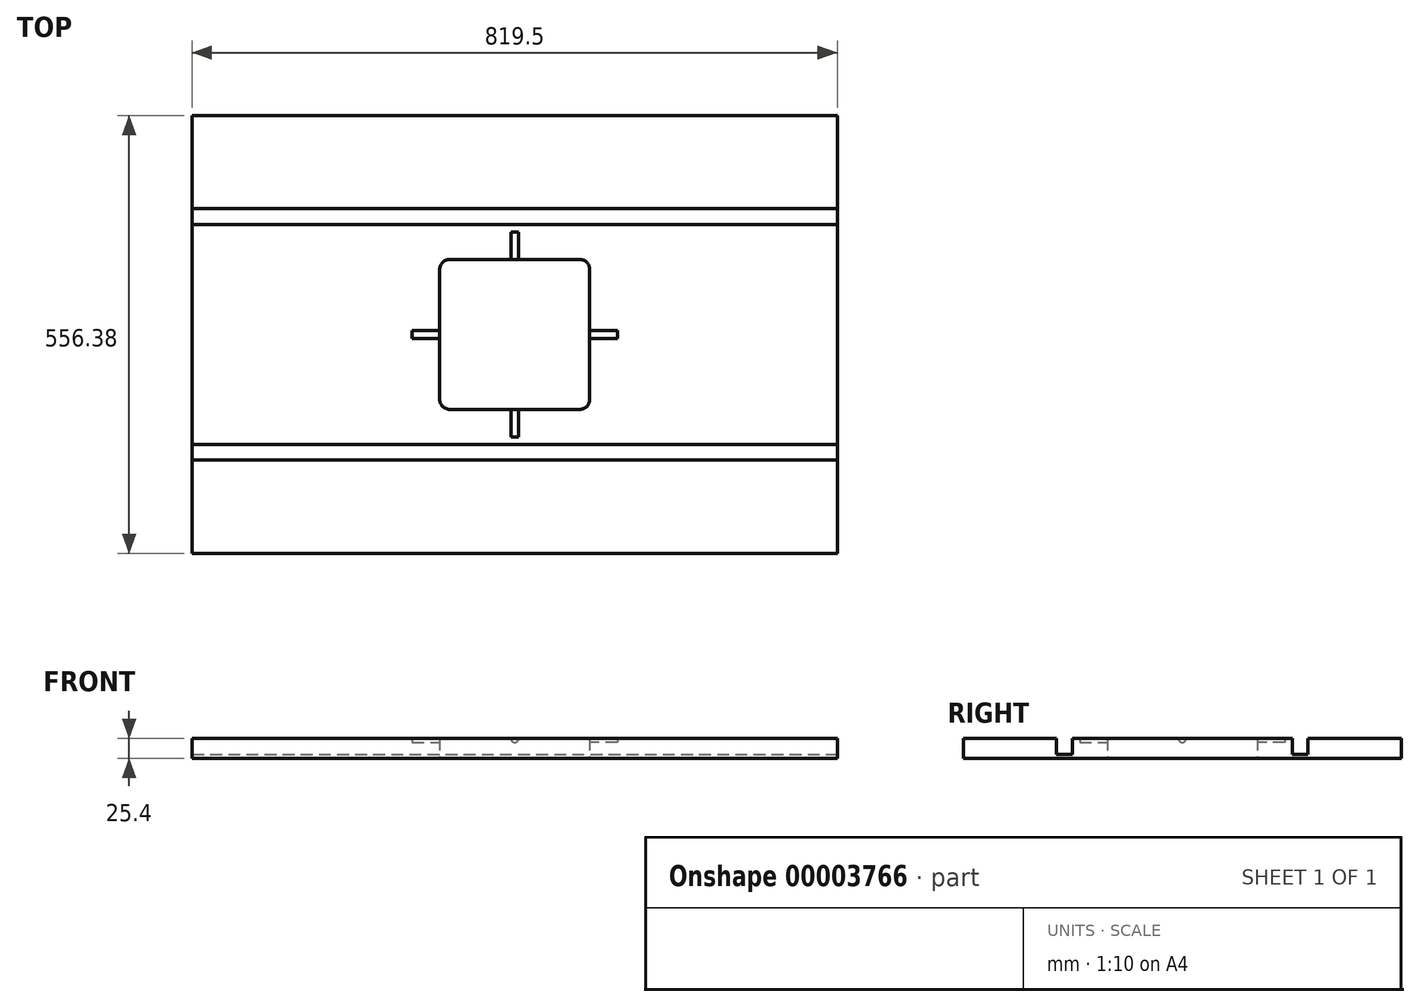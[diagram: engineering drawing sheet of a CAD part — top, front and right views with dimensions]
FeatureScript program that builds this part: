
annotation { "Feature Type Name" : "Feature", "Feature Type Description" : "" }
export const myFeature = defineFeature(function(context is Context, id is Id, definition is map)
    precondition{}
    {
        {
            var Q0;
            Q0=qCreatedBy(makeId("Top.planeOp"),FACE);
            var sketch = newSketch(context, id + "F0", { "sketchPlane" : qUnion([Q0])});
            skLineSegment(sketch, "E0.rect.bottom", {"start": v(-82.55, 95.25) * mm, "end": v(82.55, 95.25) * mm});
            skLineSegment(sketch, "E0.rect.top", {"start": v(-82.55, -95.25) * mm, "end": v(82.55, -95.25) * mm});
            skLineSegment(sketch, "E0.rect.left", {"start": v(-95.25, 82.55) * mm, "end": v(-95.25, -82.55) * mm});
            skLineSegment(sketch, "E0.rect.right", {"start": v(95.25, 82.55) * mm, "end": v(95.25, -82.55) * mm});
            skPoint(sketch, "E0.rect.middle", {"position": v(0, 0) * mm});
            skPoint(sketch, "E1.visualSharp", {"position": v(-95.25, 95.25) * mm});
            skArc(sketch, "E1.filletArc", {"start": v(-82.55, 95.25) * mm, "mid": v(-91.53, 91.53) * mm, "end": v(-95.25, 82.55) * mm});
            skPoint(sketch, "E2.visualSharp", {"position": v(-95.25, -95.25) * mm});
            skArc(sketch, "E2.filletArc", {"start": v(-95.25, -82.55) * mm, "mid": v(-91.53, -91.53) * mm, "end": v(-82.55, -95.25) * mm});
            skPoint(sketch, "E3.visualSharp", {"position": v(95.25, 95.25) * mm});
            skArc(sketch, "E3.filletArc", {"start": v(95.25, 82.55) * mm, "mid": v(91.53, 91.53) * mm, "end": v(82.55, 95.25) * mm});
            skPoint(sketch, "E4.visualSharp", {"position": v(95.25, -95.25) * mm});
            skArc(sketch, "E4.filletArc", {"start": v(82.55, -95.25) * mm, "mid": v(91.53, -91.53) * mm, "end": v(95.25, -82.55) * mm});
            skLineSegment(sketch, "E5.rect.bottom", {"start": v(-409.75, 278.2) * mm, "end": v(409.75, 278.2) * mm});
            skLineSegment(sketch, "E5.rect.top", {"start": v(-409.75, -278.2) * mm, "end": v(409.75, -278.2) * mm});
            skLineSegment(sketch, "E5.rect.left", {"start": v(-409.75, 278.2) * mm, "end": v(-409.75, -278.2) * mm});
            skLineSegment(sketch, "E5.rect.right", {"start": v(409.75, 278.2) * mm, "end": v(409.75, -278.2) * mm});
            skLineSegment(sketch, "E6", {"start": v(0, -95.25) * mm, "end": v(0, 95.25) * mm, "construction": true});
            skLineSegment(sketch, "E7", {"start": v(0, 0) * mm, "end": v(-95.25, 0) * mm, "construction": true});
            skLineSegment(sketch, "E8", {"start": v(0, 0) * mm, "end": v(95.25, 0) * mm, "construction": true});
            skSolve(sketch);
        }
        {
            var Q0;
            Q0=makeQuery(id+"F0.imprint","IMPRINT",FACE,{"disambiguationData":[TD([[makeQuery(id+"F0.imprint","IMPRINT",EDGE,{"derivedFrom":sQuery(id+"F0.wireOp",EDGE,"E0.rect.bottom")}),1.0]])]});
            extrude(context, id + "F1", {"entities" : qUnion([Q0]), "depth" : 25.4 * mm});
        }
        {
            var Q0;
            Q0=makeQuery(id+"F1.opExtrude","CAP_FACE",FACE,{"disambiguationData":[OSD([sQuery(id+"F0.wireOp",EDGE,"E0.rect.bottom"),sQuery(id+"F0.wireOp",EDGE,"E0.rect.top"),sQuery(id+"F0.wireOp",EDGE,"E0.rect.left"),sQuery(id+"F0.wireOp",EDGE,"E0.rect.right"),sQuery(id+"F0.wireOp",EDGE,"E1.filletArc"),sQuery(id+"F0.wireOp",EDGE,"E2.filletArc"),sQuery(id+"F0.wireOp",EDGE,"E3.filletArc"),sQuery(id+"F0.wireOp",EDGE,"E4.filletArc"),sQuery(id+"F0.wireOp",EDGE,"E5.rect.bottom"),sQuery(id+"F0.wireOp",EDGE,"E5.rect.top"),sQuery(id+"F0.wireOp",EDGE,"E5.rect.left"),sQuery(id+"F0.wireOp",EDGE,"E5.rect.right")])],"isStart":false});
            var sketch = newSketch(context, id + "F2", { "sketchPlane" : qUnion([Q0])});
            skLineSegment(sketch, "E9", {"start": v(-409.75, 139.7) * mm, "end": v(409.75, 139.7) * mm});
            skLineSegment(sketch, "E10.0", {"start": v(-409.75, 159.7) * mm, "end": v(409.75, 159.7) * mm});
            skLineSegment(sketch, "E11", {"start": v(0, 0) * mm, "end": v(409.75, 0) * mm, "construction": true});
            skLineSegment(sketch, "E12.0.MirrorCS", {"start": v(-409.75, -139.7) * mm, "end": v(409.75, -139.7) * mm});
            skLineSegment(sketch, "E13.0.MirrorCS", {"start": v(-409.75, -159.7) * mm, "end": v(409.75, -159.7) * mm});
            skSolve(sketch);
        }
        {
            var Q0;
            {var subQ2=sQuery(id+"F2.wireOp",EDGE,"E9");Q0=makeQuery(id+"F2.imprint","IMPRINT",FACE,{"disambiguationData":[TD([[makeQuery(id+"F2.imprint","IMPRINT",EDGE,{"derivedFrom":subQ2}),1.0]])]});}
            var Q1;
            {var subQ2=sQuery(id+"F2.wireOp",EDGE,"E12.0.MirrorCS");Q1=makeQuery(id+"F2.imprint","IMPRINT",FACE,{"disambiguationData":[TD([[makeQuery(id+"F2.imprint","IMPRINT",EDGE,{"derivedFrom":subQ2}),-1.0]])]});}
            extrude(context, id + "F3", {"entities" : qUnion([Q0, Q1]), "operationType" : NewBodyOperationType.REMOVE, "oppositeDirection" : true, "depth" : 20 * mm});
        }
        {
            var Q0;
            Q0=makeQuery(id+"F1.opExtrude","SWEPT_FACE",FACE,{"disambiguationData":[OSD([sQuery(id+"F0.wireOp",EDGE,"E0.rect.bottom")])]});
            var sketch = newSketch(context, id + "F4", { "sketchPlane" : qUnion([Q0])});
            skCircle(sketch, "E14", {"center": v(0, 25.4) * mm, "radius": 5 * mm});
            skSolve(sketch);
        }
        {
            var Q0;
            {var subQ0=makeQuery(id+"F1.opExtrude","CAP_EDGE",EDGE,{"disambiguationData":[OSD([sQuery(id+"F0.wireOp",EDGE,"E0.rect.bottom")])],"isStart":false});var subQ1=sQuery(id+"F4.wireOp",EDGE,"E14");var subQ3=makeQuery(id+"F4.imprint","INTERSECT",VERTEX,{"disambiguationData":[OD(0.0)],"derivedFrom":[subQ0,subQ1]});Q0=makeQuery(id+"F4.imprint","IMPRINT",FACE,{"disambiguationData":[TD([[makeQuery(id+"F4.imprint","IMPRINT",EDGE,{"disambiguationData":[TD([[subQ3,-1.0]])],"derivedFrom":subQ1}),1.0]])]});}
            extrude(context, id + "F5", {"entities" : qUnion([Q0]), "operationType" : NewBodyOperationType.REMOVE, "oppositeDirection" : true, "depth" : 35 * mm});
        }
        {
            var Q0;
            Q0=makeQuery(id+"F1.opExtrude","SWEPT_FACE",FACE,{"disambiguationData":[OSD([sQuery(id+"F0.wireOp",EDGE,"E0.rect.left")])]});
            var sketch = newSketch(context, id + "F6", { "sketchPlane" : qUnion([Q0])});
            skCircle(sketch, "E15", {"center": v(0, 25.4) * mm, "radius": 5 * mm});
            skSolve(sketch);
        }
        {
            var Q0;
            {var subQ0=makeQuery(id+"F1.opExtrude","CAP_EDGE",EDGE,{"disambiguationData":[OSD([sQuery(id+"F0.wireOp",EDGE,"E0.rect.left")])],"isStart":false});var subQ1=sQuery(id+"F6.wireOp",EDGE,"E15");var subQ3=makeQuery(id+"F6.imprint","INTERSECT",VERTEX,{"disambiguationData":[OD(0.0)],"derivedFrom":[subQ0,subQ1]});Q0=makeQuery(id+"F6.imprint","IMPRINT",FACE,{"disambiguationData":[TD([[makeQuery(id+"F6.imprint","IMPRINT",EDGE,{"disambiguationData":[TD([[subQ3,1.0]])],"derivedFrom":subQ1}),1.0]])]});}
            extrude(context, id + "F7", {"entities" : qUnion([Q0]), "operationType" : NewBodyOperationType.REMOVE, "oppositeDirection" : true, "depth" : 35 * mm});
        }
        {
            var Q0;
            Q0=makeQuery(id+"F1.opExtrude","SWEPT_FACE",FACE,{"disambiguationData":[OSD([sQuery(id+"F0.wireOp",EDGE,"E0.rect.top")])]});
            var sketch = newSketch(context, id + "F8", { "sketchPlane" : qUnion([Q0])});
            skCircle(sketch, "E16", {"center": v(0, 25.4) * mm, "radius": 5 * mm});
            skSolve(sketch);
        }
        {
            var Q0;
            {var subQ0=makeQuery(id+"F1.opExtrude","CAP_EDGE",EDGE,{"disambiguationData":[OSD([sQuery(id+"F0.wireOp",EDGE,"E0.rect.top")])],"isStart":false});var subQ1=sQuery(id+"F8.wireOp",EDGE,"E16");var subQ3=makeQuery(id+"F8.imprint","INTERSECT",VERTEX,{"disambiguationData":[OD(0.0)],"derivedFrom":[subQ0,subQ1]});Q0=makeQuery(id+"F8.imprint","IMPRINT",FACE,{"disambiguationData":[TD([[makeQuery(id+"F8.imprint","IMPRINT",EDGE,{"disambiguationData":[TD([[subQ3,1.0]])],"derivedFrom":subQ1}),1.0]])]});}
            extrude(context, id + "F9", {"entities" : qUnion([Q0]), "operationType" : NewBodyOperationType.REMOVE, "oppositeDirection" : true, "depth" : 35 * mm});
        }
        {
            var Q0;
            Q0=makeQuery(id+"F1.opExtrude","SWEPT_FACE",FACE,{"disambiguationData":[OSD([sQuery(id+"F0.wireOp",EDGE,"E0.rect.right")])]});
            var sketch = newSketch(context, id + "F10", { "sketchPlane" : qUnion([Q0])});
            skCircle(sketch, "E17", {"center": v(0, 25.4) * mm, "radius": 5 * mm});
            skSolve(sketch);
        }
        {
            var Q0;
            {var subQ0=makeQuery(id+"F1.opExtrude","CAP_EDGE",EDGE,{"disambiguationData":[OSD([sQuery(id+"F0.wireOp",EDGE,"E0.rect.right")])],"isStart":false});var subQ1=sQuery(id+"F10.wireOp",EDGE,"E17");var subQ3=makeQuery(id+"F10.imprint","INTERSECT",VERTEX,{"disambiguationData":[OD(0.0)],"derivedFrom":[subQ0,subQ1]});Q0=qUnion([makeQuery(id+"F10.imprint","IMPRINT",FACE,{"disambiguationData":[TD([[makeQuery(id+"F10.imprint","IMPRINT",EDGE,{"disambiguationData":[TD([[subQ3,1.0]])],"derivedFrom":subQ1}),1.0]])]}),makeQuery(id+"F10.imprint","IMPRINT",FACE,{"disambiguationData":[TD([[makeQuery(id+"F10.imprint","IMPRINT",EDGE,{"disambiguationData":[TD([[subQ3,-1.0]])],"derivedFrom":subQ1}),1.0]])]})]);}
            extrude(context, id + "F11", {"entities" : qUnion([Q0]), "operationType" : NewBodyOperationType.REMOVE, "oppositeDirection" : true, "depth" : 35 * mm});
        }
    });
